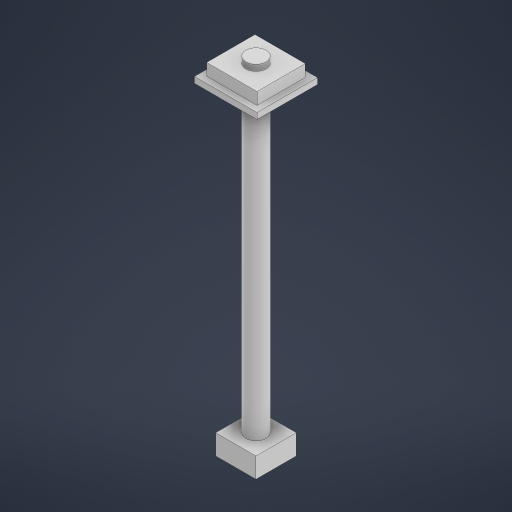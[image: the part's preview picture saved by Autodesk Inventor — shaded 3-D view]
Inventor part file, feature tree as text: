
AUTODESK INVENTOR PART (.ipt)
format: ipt  version: 2024 (Build 280153000, 153)  size: 245,248 bytes
history: native  units: mm
features: extrude x6, sketch x6, other x4
ambient origin geometry x8: Origin, YZ Plane, XZ Plane, XY Plane, X Axis, Y Axis, Z Axis, Center Point
bodies: Body1 (feature_tree), Body2 (feature_tree), Body3 (feature_tree), Body4 (feature_tree)
feature tree (16):
  other  "솔리드1"
  extrude  "돌출1"  Depth=25.0mm
  extrude  "돌출2"  Depth=24.0mm
  extrude  "돌출3"  Depth=9.0mm TaperAngle=0.0deg
  extrude  "돌출4"  Depth=3.0mm TaperAngle=0.0deg
  extrude  "돌출5"  Depth=3.0mm
  extrude  "돌출6"  Depth=3.0mm
  sketch  "스케치1"
  sketch  "스케치2"
  sketch  "스케치3"
  other  "솔리드2"
  sketch  "스케치4"
  other  "솔리드3"
  sketch  "스케치5"
  other  "솔리드4"
  sketch  "스케치6"
